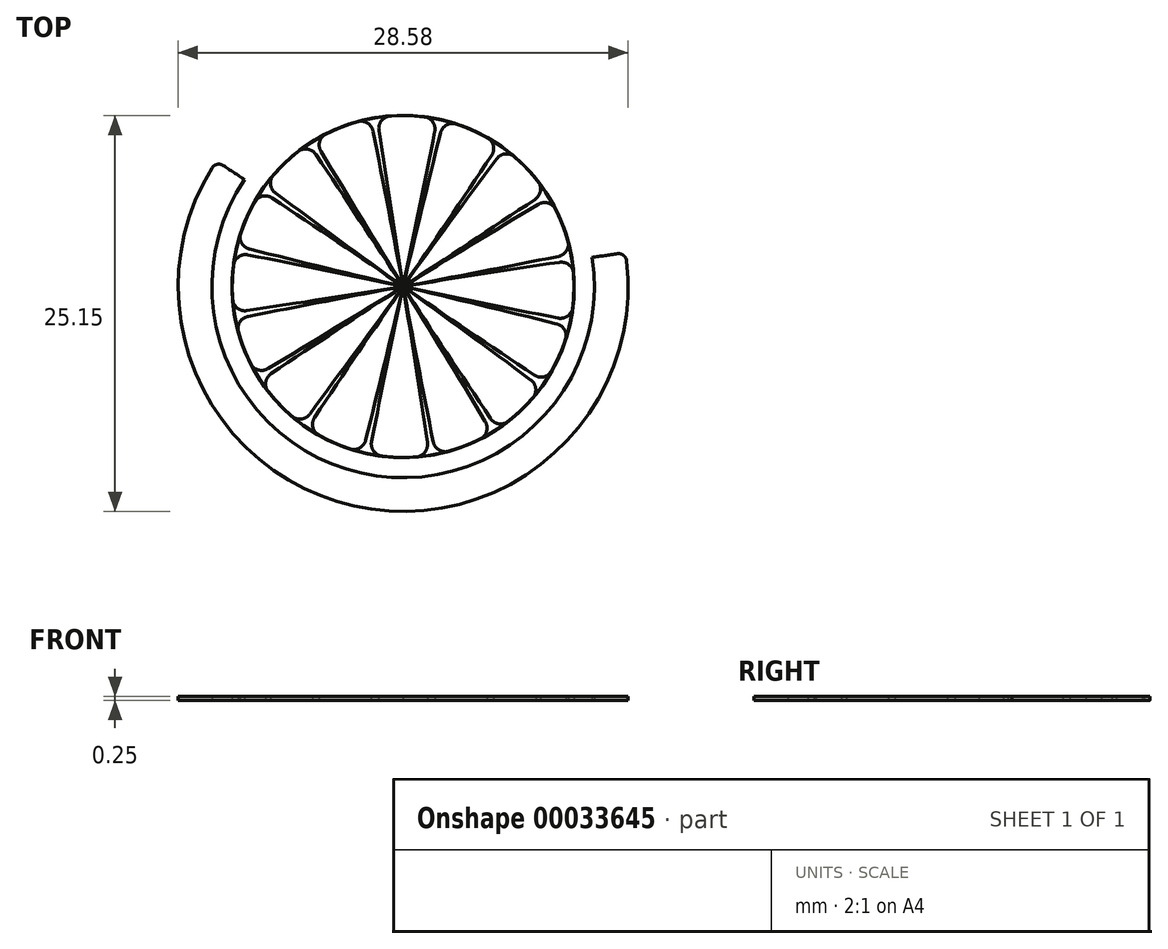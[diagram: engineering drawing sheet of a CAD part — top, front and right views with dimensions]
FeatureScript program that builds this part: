
annotation { "Feature Type Name" : "Feature", "Feature Type Description" : "" }
export const myFeature = defineFeature(function(context is Context, id is Id, definition is map)
    precondition{}
    {
        {
            assignVariable(context, id + "F0", {"name" : "N", "anyValue" : 16});
        }
        {
            assignVariable(context, id + "F1", {"name" : "Swid", "anyValue" : 0.25});
        }
        {
            var Q0;
            Q0=qCreatedBy(makeId("Top.planeOp"),FACE);
            var sketch = newSketch(context, id + "F2", { "sketchPlane" : qUnion([Q0])});
            skCircle(sketch, "E0", {"center": v(0, 0) * mm, "radius": 12.15 * mm, "construction": true});
            skCircle(sketch, "E1", {"center": v(0, 0) * mm, "radius": 12.7 * mm, "construction": true});
            skCircle(sketch, "E2", {"center": v(0, 0) * mm, "radius": 14.29 * mm});
            skLineSegment(sketch, "E3", {"start": v(0, 0) * mm, "end": v(0, 12.15) * mm, "construction": true});
            skLineSegment(sketch, "E4", {"start": v(0, 0) * mm, "end": v(0.8, 12.12) * mm, "construction": true});
            skLineSegment(sketch, "E5", {"start": v(0, 0) * mm, "end": v(1.59, 12.04) * mm, "construction": true});
            skLineSegment(sketch, "E6", {"start": v(0, 0) * mm, "end": v(2.37, 11.91) * mm, "construction": true});
            skLineSegment(sketch, "E7", {"start": v(0, 0) * mm, "end": v(3.14, 11.73) * mm, "construction": true});
            skCircle(sketch, "E8", {"center": v(0, 0) * mm, "radius": 10.86 * mm});
            skLineSegment(sketch, "E9", {"start": v(0.8, 12.12) * mm, "end": v(0, 12.17) * mm, "construction": true});
            skLineSegment(sketch, "E10", {"start": v(1.59, 12.04) * mm, "end": v(0, 12.25) * mm, "construction": true});
            skLineSegment(sketch, "E11", {"start": v(2.37, 11.91) * mm, "end": v(0.03, 12.38) * mm, "construction": true});
            skLineSegment(sketch, "E12", {"start": v(3.14, 11.73) * mm, "end": v(0.07, 12.55) * mm, "construction": true});
            skLineSegment(sketch, "E13", {"start": v(0, 0) * mm, "end": v(3.9, 11.5) * mm, "construction": true});
            skLineSegment(sketch, "E14", {"start": v(3.9, 11.5) * mm, "end": v(0.14, 12.78) * mm, "construction": true});
            skLineSegment(sketch, "E15", {"start": v(0, 0) * mm, "end": v(4.65, 11.22) * mm, "construction": true});
            skLineSegment(sketch, "E16", {"start": v(0, 0) * mm, "end": v(5.37, 10.9) * mm, "construction": true});
            skLineSegment(sketch, "E17", {"start": v(0, 0) * mm, "end": v(6.07, 10.52) * mm, "construction": true});
            skLineSegment(sketch, "E18", {"start": v(4.65, 11.22) * mm, "end": v(0.24, 13.05) * mm, "construction": true});
            skLineSegment(sketch, "E19", {"start": v(5.37, 10.9) * mm, "end": v(0.38, 13.35) * mm, "construction": true});
            skLineSegment(sketch, "E20", {"start": v(6.07, 10.52) * mm, "end": v(0.57, 13.7) * mm, "construction": true});
            skLineSegment(sketch, "E21", {"start": v(0, 0) * mm, "end": v(6.75, 10.1) * mm, "construction": true});
            skLineSegment(sketch, "E22", {"start": v(0, 0) * mm, "end": v(7.4, 9.64) * mm, "construction": true});
            skLineSegment(sketch, "E23", {"start": v(0, 0) * mm, "end": v(8, 9.13) * mm, "construction": true});
            skLineSegment(sketch, "E24", {"start": v(0, 0) * mm, "end": v(8.59, 8.59) * mm, "construction": true});
            skLineSegment(sketch, "E25", {"start": v(0, 0) * mm, "end": v(9.13, 8) * mm, "construction": true});
            skLineSegment(sketch, "E26", {"start": v(6.75, 10.1) * mm, "end": v(0.8, 14.07) * mm, "construction": true});
            skLineSegment(sketch, "E27", {"start": v(7.4, 9.64) * mm, "end": v(1.09, 14.47) * mm, "construction": true});
            skLineSegment(sketch, "E28", {"start": v(8, 9.13) * mm, "end": v(1.43, 14.9) * mm, "construction": true});
            skLineSegment(sketch, "E29", {"start": v(8.59, 8.59) * mm, "end": v(1.84, 15.33) * mm, "construction": true});
            skLineSegment(sketch, "E30", {"start": v(9.13, 8) * mm, "end": v(2.32, 15.78) * mm, "construction": true});
            skLineSegment(sketch, "E31", {"start": v(0, 0) * mm, "end": v(9.64, 7.4) * mm, "construction": true});
            skLineSegment(sketch, "E32", {"start": v(9.64, 7.4) * mm, "end": v(2.86, 16.22) * mm, "construction": true});
            skLineSegment(sketch, "E33", {"start": v(0, 0) * mm, "end": v(10.1, 6.75) * mm, "construction": true});
            skLineSegment(sketch, "E34", {"start": v(10.1, 6.75) * mm, "end": v(3.47, 16.66) * mm, "construction": true});
            skSolve(sketch);
        }
        {
            var Q0;
            Q0=qCreatedBy(makeId("Top.planeOp"),FACE);
            var sketch = newSketch(context, id + "F3", { "sketchPlane" : qUnion([Q0])});
            skLineSegment(sketch, "E35.0", {"start": v(9.64, 7.4) * mm, "end": v(2.86, 16.22) * mm, "construction": true});
            skLineSegment(sketch, "E35.1", {"start": v(9.13, 8) * mm, "end": v(2.32, 15.78) * mm, "construction": true});
            skLineSegment(sketch, "E35.2", {"start": v(8.59, 8.59) * mm, "end": v(1.84, 15.33) * mm, "construction": true});
            skLineSegment(sketch, "E35.3", {"start": v(8, 9.13) * mm, "end": v(1.43, 14.9) * mm, "construction": true});
            skLineSegment(sketch, "E35.4", {"start": v(7.4, 9.64) * mm, "end": v(1.09, 14.47) * mm, "construction": true});
            skLineSegment(sketch, "E35.5", {"start": v(6.75, 10.1) * mm, "end": v(0.8, 14.07) * mm, "construction": true});
            skLineSegment(sketch, "E35.6", {"start": v(6.07, 10.52) * mm, "end": v(0.57, 13.7) * mm, "construction": true});
            skLineSegment(sketch, "E35.7", {"start": v(5.37, 10.9) * mm, "end": v(0.38, 13.35) * mm, "construction": true});
            skLineSegment(sketch, "E35.8", {"start": v(4.65, 11.22) * mm, "end": v(0.24, 13.05) * mm, "construction": true});
            skLineSegment(sketch, "E35.9", {"start": v(3.9, 11.5) * mm, "end": v(0.14, 12.78) * mm, "construction": true});
            skLineSegment(sketch, "E35.10", {"start": v(3.14, 11.73) * mm, "end": v(0.07, 12.55) * mm, "construction": true});
            skLineSegment(sketch, "E35.11", {"start": v(2.37, 11.91) * mm, "end": v(0.03, 12.38) * mm, "construction": true});
            skLineSegment(sketch, "E35.12", {"start": v(1.59, 12.04) * mm, "end": v(0, 12.25) * mm, "construction": true});
            skLineSegment(sketch, "E35.13", {"start": v(0.8, 12.12) * mm, "end": v(0, 12.17) * mm, "construction": true});
            skCircle(sketch, "E35.14", {"center": v(0, 0) * mm, "radius": 12.15 * mm});
            skCircle(sketch, "E35.15", {"center": v(0, 0) * mm, "radius": 10.86 * mm});
            skCircle(sketch, "E35.16", {"center": v(0, 0) * mm, "radius": 12.7 * mm, "construction": true});
            skCircle(sketch, "E35.17", {"center": v(0, 0) * mm, "radius": 14.29 * mm});
            skLineSegment(sketch, "E36.0", {"start": v(10.1, 6.75) * mm, "end": v(3.47, 16.66) * mm, "construction": true});
            skLineSegment(sketch, "E37.0", {"start": v(0, 0) * mm, "end": v(0, 12.15) * mm, "construction": true});
            skFitSpline(sketch, "E38", {"points": [v(0, 20.8) * mm, v(0.04, 21.12) * mm, v(0.3, 22.04) * mm, v(0.97, 23.47) * mm, v(2.25, 25.28) * mm, v(4.27, 27.28) * mm, v(7.12, 29.27) * mm, v(10.86, 31) * mm, v(15.45, 32.22) * mm, v(20.8, 32.68) * mm, v(26.8, 32.15) * mm, v(33.21, 30.42) * mm, v(39.8, 27.34) * mm, v(46.28, 22.79) * mm, v(52.32, 16.74) * mm, v(57.58, 9.22) * mm, v(0, 0) * mm], "startDerivative": vector(7.54, 64.54) * mm, "endDerivative": vector(-870.75, -139.39) * mm});
            skLineSegment(sketch, "E39", {"start": v(2.27, 25.3) * mm, "end": v(0, 0) * mm, "construction": true});
            skLineSegment(sketch, "E40", {"start": v(0, 0) * mm, "end": v(6.47, 28.92) * mm, "construction": true});
            skFitSpline(sketch, "E41.MirrorCS", {"points": [v(8.87, 18.82) * mm, v(8.97, 19.12) * mm, v(9.13, 20.06) * mm, v(9.13, 21.64) * mm, v(8.74, 23.82) * mm, v(7.77, 26.5) * mm, v(6.04, 29.52) * mm, v(3.4, 32.67) * mm, v(-0.23, 35.73) * mm, v(-4.89, 38.43) * mm, v(-10.53, 40.5) * mm, v(-17.07, 41.68) * mm, v(-24.35, 41.7) * mm, v(-32.15, 40.35) * mm, v(-40.19, 37.45) * mm, v(-48.15, 32.89) * mm, v(0, 0) * mm], "startDerivative": vector(20.7, 61.6) * mm, "endDerivative": vector(728.2, -497.34) * mm});
            skLineSegment(sketch, "E42", {"start": v(8.87, 18.82) * mm, "end": v(8.74, 18.55) * mm});
            skLineSegment(sketch, "E43", {"start": v(0, 20.81) * mm, "end": v(0, 20.5) * mm});
            skSolve(sketch);
        }
        {
            var Q0;
            {var subQ3=sQuery(id+"F3.wireOp",EDGE,"E41.MirrorCS");var subQ6=sQuery(id+"F3.wireOp",EDGE,"E35.17");var subQ8=makeQuery(id+"F3.imprint","INTERSECT",VERTEX,{"disambiguationData":[OD(1.0)],"derivedFrom":[subQ6,subQ3]});Q0=makeQuery(id+"F3.imprint","IMPRINT",FACE,{"disambiguationData":[TD([[makeQuery(id+"F3.imprint","IMPRINT",EDGE,{"disambiguationData":[TD([[subQ8,-1.0]])],"derivedFrom":subQ6}),1.0]])]});}
            var Q1;
            {var subQ3=sQuery(id+"F3.wireOp",EDGE,"E41.MirrorCS");var subQ5=sQuery(id+"F3.wireOp",EDGE,"E35.15");var subQ6=makeQuery(id+"F3.imprint","INTERSECT",VERTEX,{"derivedFrom":[subQ5,subQ3]});Q1=makeQuery(id+"F3.imprint","IMPRINT",FACE,{"disambiguationData":[TD([[makeQuery(id+"F3.imprint","IMPRINT",EDGE,{"disambiguationData":[TD([[subQ6,-1.0]])],"derivedFrom":subQ5}),1.0]])]});}
            var Q2;
            {var subQ2=sQuery(id+"F3.wireOp",EDGE,"E42");Q2=makeQuery(id+"F3.imprint","IMPRINT",FACE,{"disambiguationData":[TD([[makeQuery(id+"F3.imprint","IMPRINT",EDGE,{"derivedFrom":subQ2}),-1.0]])]});}
            extrude(context, id + "F4", {"entities" : qUnion([Q0, Q1, Q2]), "depth" : (getVariable(context, 'Swid')) * mm, "offsetDistance" : 25.4 * mm});
        }
        {
            var Q0;
            Q0=qCreatedBy(makeId("Right.planeOp"),FACE);
            var sketch = newSketch(context, id + "F5", { "sketchPlane" : qUnion([Q0])});
            skLineSegment(sketch, "E44", {"start": v(0, 0) * mm, "end": v(0, 43.3) * mm, "construction": true});
            skSolve(sketch);
        }
        {
            var Q0;
            Q0=makeQuery(id+"F4.opExtrude","SWEPT_EDGE",EDGE,{"disambiguationData":[OSD([sQuery(id+"F3.wireOp",EDGE,"E35.17"),sQuery(id+"F3.wireOp",EDGE,"E41.MirrorCS")])]});
            var Q1;
            Q1=makeQuery(id+"F4.opExtrude","SWEPT_EDGE",EDGE,{"disambiguationData":[OSD([sQuery(id+"F3.wireOp",EDGE,"E35.17"),sQuery(id+"F3.wireOp",EDGE,"E38")])]});
            fillet(context, id + "F6", {"entities" : qUnion([Q0, Q1]), "radius" : 0.5 * mm, "tangentPropagation" : true, "allowEdgeOverflow" : false});
        }
        {
            var Q0;
            Q0=makeQuery(id+"F4.opExtrude","SWEPT_EDGE",EDGE,{"disambiguationData":[OSD([sQuery(id+"F3.wireOp",EDGE,"E35.15"),sQuery(id+"F3.wireOp",EDGE,"E42")])]});
            var Q1;
            Q1=makeQuery(id+"F4.opExtrude","SWEPT_EDGE",EDGE,{"disambiguationData":[OSD([sQuery(id+"F3.wireOp",EDGE,"E35.15"),sQuery(id+"F3.wireOp",EDGE,"E43")])]});
            fillet(context, id + "F7", {"entities" : qUnion([Q0, Q1]), "radius" : 0.8 * mm, "tangentPropagation" : true, "allowEdgeOverflow" : false});
        }
        {
            var Q0;
            Q0=makeQuery(id+"F4.opExtrude","SWEPT_BODY",BODY,{"disambiguationData":[OSD([sQuery(id+"F3.wireOp",EDGE,"E35.15"),sQuery(id+"F3.wireOp",EDGE,"E35.17"),sQuery(id+"F3.wireOp",EDGE,"E38"),sQuery(id+"F3.wireOp",EDGE,"E41.MirrorCS"),sQuery(id+"F3.wireOp",EDGE,"9305e2c8-a00a-4cbc-a3b2-8fc88bc1717c"),sQuery(id+"F3.wireOp",EDGE,"f762f43d-eaf9-45ff-b6cd-062fd530227c")])]});
            var Q1;
            Q1=sQuery(id+"F5.wireOp",EDGE,"E44");
            circularPattern(context, id + "F8", {"operationType" : NewBodyOperationType.ADD, "entities" : qUnion([Q0]), "axis" : qUnion([Q1]), "angle" : (360 / getVariable(context, 'N')) * degree, "instanceCount" : getVariable(context, 'N'), "oppositeDirection" : true});
        }
    });
